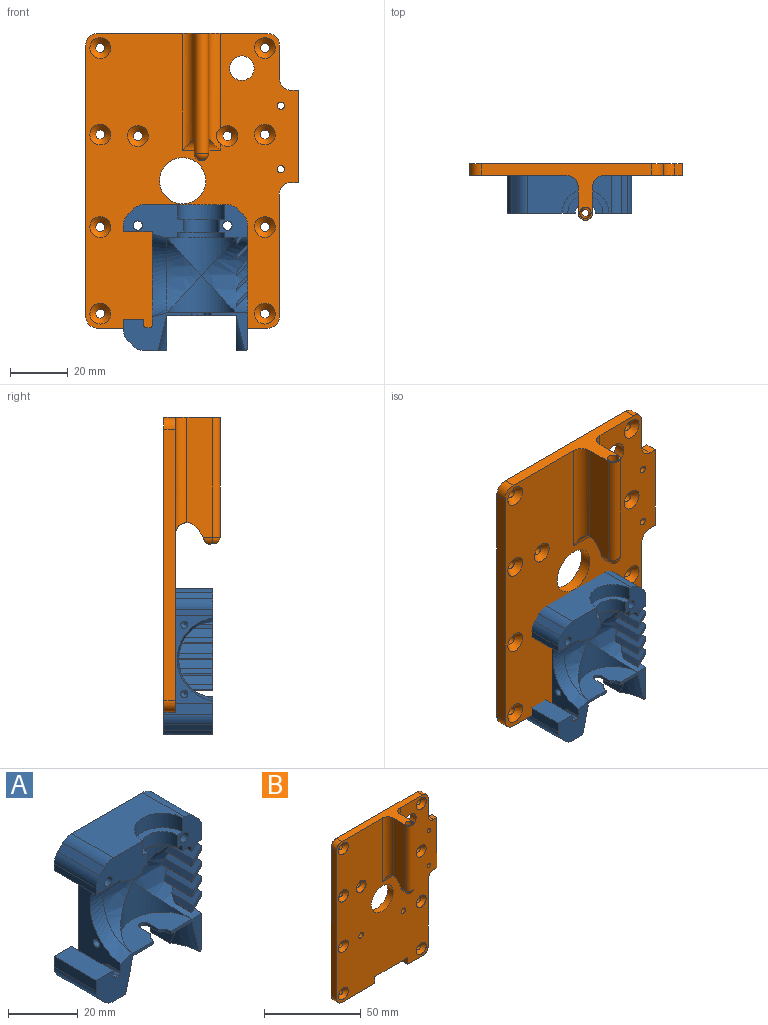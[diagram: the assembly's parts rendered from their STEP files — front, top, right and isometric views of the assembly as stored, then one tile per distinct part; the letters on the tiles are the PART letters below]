
ASSEMBLY  parts=2 mates=1
PART A: 86 faces, bbox 47x25.3x54.5 mm
  f0: cone r=0mm half-angle=59deg, axis (-1,0,0), area 5.7mm2, adj f9
  f1: cone r=0mm half-angle=59deg, axis (-1,0,0), area 5.7mm2, adj f10
  f2: plane 6.9x1mm, normal (0,1,0), area 6.9mm2, adj f8,f12,f15,f43
  f3: cylinder r=12mm len=24mm, axis (0,0,1), area 245mm2, adj f11,f20,f77
  f4: cylinder r=12mm len=24mm, axis (0,0,1), area 245mm2, adj f11,f65,f77
  f5: plane 4.29x1mm, normal (1,0,0), area 4.3mm2, adj f6,f17,f18,f20
  f6: cylinder r=1.6mm len=3.2mm, axis (0,0,1), area 5mm2, adj f5,f7,f17,f20
  f7: plane 4.29x1mm, normal (-1,0,0), area 4.3mm2, adj f6,f17,f19,f20
  f8: cylinder r=1mm len=6.9mm, axis (0,0,1), area 10.8mm2, adj f2,f27,f41,f43
  f9: cylinder r=1.25mm len=5mm, axis (-1,0,0), area 39.3mm2, adj f0,f41
  f10: cylinder r=1.25mm len=5mm, axis (-1,0,0), area 39.3mm2, adj f1,f41
  f11: extruded ~26x12mm, area 239.5mm2, adj f3,f4,f33
  f12: cylinder r=1mm len=1mm, axis (1,0,0), area 1.6mm2, adj f2,f26,f27,f40
  f13: plane 20.95x15.95mm, normal (1,0,0), area 133.6mm2, adj f17,f23,f31,f43
  f14: plane 20.95x15.95mm, normal (-1,0,0), area 133.6mm2, adj f17,f23,f24,f25
  f15: cylinder r=1mm len=6.9mm, axis (0,0,1), area 10.8mm2, adj f2,f26,f35,f38,f43
  f16: plane 10.9x7mm, normal (0,1,0), area 62.7mm2, adj f34,f35,f36,f38,f42,f76
  f17: plane 24x17mm, normal (0,0,-1), area 371.9mm2, adj f5,f6,f7,f13,f14,f18,f19,f23
  f18: cylinder r=3.5mm len=3.11mm, axis (0,0,1), area 3.8mm2, adj f5,f17,f20,f83
  f19: cylinder r=3.5mm len=3.11mm, axis (0,0,1), area 3.8mm2, adj f7,f17,f20,f84
  f20: plane 24x12mm, normal (0,0,1), area 190mm2, adj f3,f5,f6,f7,f18,f19,f83,f84
  f21: cylinder r=1.6mm len=17mm, axis (0,1,0), area 170.9mm2, adj f23,f85
  f22: cylinder r=1.6mm len=17mm, axis (0,1,0), area 170.9mm2, adj f23,f82
  f23: plane 50.5x43mm, normal (0,1,0), area 1429mm2, adj f13,f14,f17,f21,f22,f25,f32,f41
  f24: cone r=12mm half-angle=14deg, axis (0,0,-1), area 55.7mm2, adj f14,f25,f84
  f25: plane 17x3mm, normal (0,0,-1), area 32.6mm2, adj f14,f23,f24,f44
  f26: torus R=2mm, axis (1,0,0), area 3.4mm2, adj f12,f15,f37,f38
  f27: torus R=2mm, axis (-1,0,0), area 3.4mm2, adj f8,f12,f39,f41
  f28: plane 6.65x2.17mm, normal (0.71,0,-0.71), area 13.8mm2, adj f29,f77,f82
  f29: plane 6.64x1.41mm, normal (-1,0,0), area 7.7mm2, adj f28,f30,f77,f82
  f30: plane 4.41x1.13mm, normal (-0.71,0,0.71), area 2.9mm2, adj f29,f77,f82
  f31: cone r=12mm half-angle=14deg, axis (0,0,-1), area 55.7mm2, adj f13,f43,f83
  f32: plane 17x10mm, normal (0,0,-1), area 170mm2, adj f23,f41,f75,f85
  f33: bspline ~28.84x16.7mm, area 203.5mm2, adj f11,f41,f83,f85
  f34: cylinder r=5mm len=17mm, axis (0,-1,0), area 66.8mm2, adj f16,f36,f42,f83
  f35: cylinder r=5mm len=17mm, axis (0,1,0), area 66mm2, adj f15,f16,f36,f38,f43,f83
  f36: plane 17x2.07mm, normal (-0.71,0,-0.71), area 49.8mm2, adj f16,f34,f35,f83
  f37: cylinder r=1mm len=5mm, axis (0,1,0), area 7.9mm2, adj f26,f38,f40,f83
  f38: plane 17x10.9mm, normal (1,0,0), area 123.9mm2, adj f15,f16,f26,f35,f37,f76,f83
  f39: cylinder r=1mm len=5mm, axis (0,1,0), area 7.9mm2, adj f27,f40,f41,f83
  f40: plane 5x1mm, normal (0,0,1), area 5mm2, adj f12,f37,f39,f83
  f41: plane 41.1x17.03mm, normal (-1,0,0), area 357.9mm2, adj f8,f9,f10,f23,f27,f32,f33,f39
  f42: plane 17x3.83mm, normal (-1,0,0), area 65.1mm2, adj f16,f34,f76,f83
  f43: plane 17x7.93mm, normal (0,0,-1), area 84.6mm2, adj f2,f8,f13,f15,f23,f31,f35,f41
  f44: cylinder r=1mm len=17mm, axis (0,-1,0), area 26.7mm2, adj f23,f25,f64,f84
  f45: plane 10.55x4.34mm, normal (0.71,0,-0.71), area 49.1mm2, adj f48,f64,f77,f78
  f46: plane 8.95x1.74mm, normal (-0.92,0,0.38), area 15mm2, adj f47,f48,f77,f78
  f47: plane 11.04x3.42mm, normal (-0.71,0,0.71), area 46.7mm2, adj f46,f64,f77,f78
  f48: plane 7.18x0.41mm, normal (-1,0,0), area 2.9mm2, adj f45,f46,f77,f78
  f49: plane 11.62x1.72mm, normal (-0.92,0,0.38), area 21mm2, adj f50,f52,f77,f79
  f50: plane 12.02x3.31mm, normal (-0.71,0,0.71), area 55.3mm2, adj f49,f64,f77,f79
  f51: plane 11.99x4.07mm, normal (0.71,0,-0.71), area 65.2mm2, adj f52,f64,f77,f79
  f52: plane 11.08x0.41mm, normal (-1,0,0), area 4.6mm2, adj f49,f51,f77,f79
  f53: plane 12.04x4.04mm, normal (0.71,0,-0.71), area 66.8mm2, adj f55,f64,f77,f80
  f54: plane 12x1.71mm, normal (-0.92,0,0.38), area 22.1mm2, adj f55,f56,f77,f80
  f55: plane 12x0.41mm, normal (-1,0,0), area 5mm2, adj f53,f54,f77,f80
  f56: plane 11.89x3.34mm, normal (-0.71,0,0.71), area 53.3mm2, adj f54,f64,f77,f80
  f57: plane 11.12x4.21mm, normal (0.71,0,-0.71), area 55.3mm2, adj f59,f64,f77,f81
  f58: plane 10.74x1.72mm, normal (-0.92,0,0.38), area 19mm2, adj f59,f60,f77,f81
  f59: plane 10.91x0.41mm, normal (-1,0,0), area 4.5mm2, adj f57,f58,f77,f81
  f60: plane 10.03x3.55mm, normal (-0.71,0,0.71), area 39.1mm2, adj f58,f64,f77,f81
  f61: cylinder r=5mm len=17mm, axis (0,1,0), area 66.8mm2, adj f23,f63,f64,f82
  f62: cylinder r=5mm len=17mm, axis (0,-1,0), area 66.8mm2, adj f23,f63,f74,f82
  f63: plane 17x2.07mm, normal (0.71,0,0.71), area 49.8mm2, adj f23,f61,f62,f82
  f64: plane 42.43x17mm, normal (1,0,0), area 534.6mm2, adj f23,f44,f45,f47,f50,f51,f53,f56
  f65: plane 24x12mm, normal (0,0,-1), area 123.1mm2, adj f4,f67,f82,f85
  f66: plane 16.2x8.1mm, normal (0,0,-1), area 44.6mm2, adj f67,f68,f82,f85
  f67: cylinder r=8.1mm len=16.2mm, axis (0,0,1), area 50.9mm2, adj f65,f66,f82,f85
  f68: cylinder r=6.1mm len=12.2mm, axis (0,0,1), area 86.2mm2, adj f66,f69,f82,f85
  f69: plane 16.2x8.1mm, normal (0,0,1), area 44.6mm2, adj f68,f70,f82,f85
  f70: cylinder r=8.1mm len=16.2mm, axis (0,0,1), area 127.2mm2, adj f69,f74,f82,f85
  f71: cylinder r=5mm len=17mm, axis (0,-1,0), area 66.8mm2, adj f23,f73,f74,f85
  f72: cylinder r=5mm len=17mm, axis (0,-1,0), area 66.8mm2, adj f23,f73,f75,f85
  f73: plane 17x2.07mm, normal (-0.71,0,0.71), area 49.8mm2, adj f23,f71,f72,f85
  f74: plane 28.86x17mm, normal (0,0,1), area 387.5mm2, adj f23,f62,f70,f71,f82,f85
  f75: plane 17x2.33mm, normal (-1,0,0), area 39.6mm2, adj f23,f32,f72,f85
  f76: plane 17x7mm, normal (0,0,1), area 119mm2, adj f16,f38,f42,f83
  f77: extruded ~26x16mm, area 298.8mm2, adj f3,f4,f28,f29,f30,f45,f46,f47
  f78: plane 5.41x4mm, normal (0,-1,0), area 5.3mm2, adj f45,f46,f47,f48,f64
  f79: plane 5.41x4mm, normal (0,-1,0), area 5.3mm2, adj f49,f50,f51,f52,f64
  f80: plane 5.41x4mm, normal (0,-1,0), area 5.3mm2, adj f53,f54,f55,f56,f64
  f81: plane 5.41x4mm, normal (0,-1,0), area 5.3mm2, adj f57,f58,f59,f60,f64
  f82: plane 13.67x9.9mm, normal (0,-1,0), area 80.3mm2, adj f22,f28,f29,f30,f61,f62,f63,f64
  f83: plane 23.87x13.37mm, normal (0,-1,0), area 139mm2, adj f17,f18,f20,f31,f33,f34,f35,f36
  f84: plane 13x12.5mm, normal (0,-1,0), area 42.3mm2, adj f17,f19,f20,f24,f44,f64,f77
  f85: plane 20.91x11.51mm, normal (0,-1,0), area 180.4mm2, adj f21,f32,f33,f41,f65,f66,f67,f68
PART B: 59 faces, bbox 73.5x19.5x102 mm
  f0: cylinder r=2.5mm len=3.39mm, axis (0,-1,0), area 7.8mm2, adj f1,f49,f54,f56,f57
  f1: plane 41.5x9mm, normal (-1,0,0), area 354mm2, adj f0,f7,f49,f51,f52,f53
  f2: plane 41.5x9mm, normal (1,0,0), area 354mm2, adj f7,f49,f50,f52,f53,f55
  f3: plane 102x73.5mm, normal (0,-1,0), area 5720.8mm2, adj f4,f5,f6,f7,f8,f9,f10,f11
  f4: plane 42.41x4mm, normal (1,0,0), area 169.6mm2, adj f3,f29,f31,f48
  f5: plane 11.59x4mm, normal (1,0,0), area 46.4mm2, adj f3,f6,f31,f47
  f6: cylinder r=4mm len=4mm, axis (0,1,0), area 25.1mm2, adj f3,f5,f7,f31
  f7: plane 59x19.5mm, normal (0,0,1), area 305.8mm2, adj f1,f2,f3,f6,f8,f31,f50,f51
  f8: cylinder r=4mm len=4mm, axis (0,1,0), area 25.1mm2, adj f3,f7,f9,f31
  f9: plane 94x4mm, normal (-1,0,0), area 376mm2, adj f3,f8,f10,f31
  f10: cylinder r=4mm len=4mm, axis (0,1,0), area 25.1mm2, adj f3,f9,f11,f31
  f11: plane 24x4mm, normal (0,0,-1), area 96mm2, adj f3,f10,f12,f31
  f12: plane 4.25x4mm, normal (1,0,0), area 17mm2, adj f3,f11,f13,f31
  f13: plane 24x4mm, normal (0,0,-1), area 96mm2, adj f3,f12,f14,f31
  f14: plane 4.25x4mm, normal (-1,0,0), area 17mm2, adj f3,f13,f15,f31
  f15: plane 11x4mm, normal (0,0,-1), area 44mm2, adj f3,f14,f29,f31
  f16: cylinder r=1.6mm len=4mm, axis (0,1,0), area 40.2mm2, adj f3,f31
  f17: cylinder r=1.6mm len=4mm, axis (0,1,0), area 40.2mm2, adj f3,f31
  f18: cylinder r=1.6mm len=3.2mm, axis (0,1,0), area 20.1mm2, adj f31,f38
  f19: cylinder r=1.6mm len=3.2mm, axis (0,1,0), area 20.1mm2, adj f31,f37
  f20: cylinder r=1.6mm len=3.2mm, axis (0,1,0), area 20.1mm2, adj f31,f41
  f21: cylinder r=1.6mm len=3.2mm, axis (0,1,0), area 20.1mm2, adj f31,f36
  f22: cylinder r=1.6mm len=3.2mm, axis (0,1,0), area 20.1mm2, adj f31,f35
  f23: cylinder r=1.6mm len=3.2mm, axis (0,1,0), area 20.1mm2, adj f31,f34
  f24: cylinder r=1.6mm len=3.2mm, axis (0,1,0), area 20.1mm2, adj f31,f33
  f25: cylinder r=1.6mm len=3.2mm, axis (0,1,0), area 20.1mm2, adj f31,f32
  f26: cylinder r=1.6mm len=3.2mm, axis (0,1,0), area 20.1mm2, adj f31,f39
  f27: cylinder r=1.6mm len=3.2mm, axis (0,1,0), area 20.1mm2, adj f31,f40
  f28: cylinder r=8mm len=16mm, axis (0,1,0), area 201.1mm2, adj f3,f31
  f29: cylinder r=4mm len=4mm, axis (0,1,0), area 25.1mm2, adj f3,f4,f15,f31
  f30: cylinder r=4.25mm len=8.5mm, axis (0,1,0), area 106.8mm2, adj f3,f31
  f31: plane 102x73.5mm, normal (0,1,0), area 6569mm2, adj f4,f5,f6,f7,f8,f9,f10,f11
  f32: cone r=1.6mm half-angle=45deg, axis (0,-1,0), area 46.2mm2, adj f3,f25
  f33: cone r=1.6mm half-angle=45deg, axis (0,-1,0), area 46.2mm2, adj f3,f24
  f34: cone r=1.6mm half-angle=45deg, axis (0,-1,0), area 46.2mm2, adj f3,f23
  f35: cone r=1.6mm half-angle=45deg, axis (0,-1,0), area 46.2mm2, adj f3,f22
  f36: cone r=1.6mm half-angle=45deg, axis (0,-1,0), area 46.2mm2, adj f3,f21
  f37: cone r=1.6mm half-angle=45deg, axis (0,-1,0), area 46.2mm2, adj f3,f19
  f38: cone r=1.6mm half-angle=45deg, axis (0,-1,0), area 47.1mm2, adj f3,f18,f50
  f39: cone r=1.6mm half-angle=45deg, axis (0,-1,0), area 46.2mm2, adj f3,f26
  f40: cone r=1.6mm half-angle=45deg, axis (0,-1,0), area 46.2mm2, adj f3,f27
  f41: cone r=1.6mm half-angle=45deg, axis (0,-1,0), area 46.2mm2, adj f3,f20
  f42: plane 4x2.5mm, normal (0,0,1), area 10mm2, adj f3,f31,f43,f47
  f43: plane 32x4mm, normal (1,0,0), area 128mm2, adj f3,f31,f42,f44
  f44: plane 4x2.5mm, normal (0,0,-1), area 10mm2, adj f3,f31,f43,f48
  f45: cylinder r=1.25mm len=4mm, axis (0,-1,0), area 31.4mm2, adj f3,f31
  f46: cylinder r=1.25mm len=4mm, axis (0,-1,0), area 31.4mm2, adj f3,f31
  f47: cylinder r=4mm len=4mm, axis (0,1,0), area 25.1mm2, adj f3,f5,f31,f42
  f48: cylinder r=4mm len=4mm, axis (0,-1,0), area 25.1mm2, adj f3,f4,f31,f44
  f49: cylinder r=13.51mm len=5mm, axis (-1,0,0), area 29.2mm2, adj f0,f1,f2,f52,f55,f56
  f50: cylinder r=4mm len=40.42mm, axis (0,0,1), area 233.3mm2, adj f2,f3,f7,f38,f52
  f51: cylinder r=4mm len=40.42mm, axis (0,0,-1), area 238mm2, adj f1,f3,f7,f52
  f52: cylinder r=4mm len=13mm, axis (-1,0,0), area 65.1mm2, adj f1,f2,f3,f49,f50,f51
  f53: cylinder r=2.5mm len=41.5mm, axis (0,0,-1), area 325.9mm2, adj f1,f2,f7,f54
  f54: sphere r=2.5mm, area 17mm2, adj f0,f53,f55,f57
  f55: cylinder r=2.5mm len=3.39mm, axis (0,-1,0), area 7.8mm2, adj f2,f49,f54,f56,f57
  f56: cylinder r=2.5mm len=4.67mm, axis (-1,0,0), area 7.7mm2, adj f0,f49,f55,f57
  f57: cylinder r=1.25mm len=23.95mm, axis (0,0,1), area 186.6mm2, adj f0,f54,f55,f56,f58
  f58: cone r=1.25mm half-angle=2deg, axis (0,0,1), area 201.1mm2, adj f7,f57
PLACE A t=(-138.01,-286.8,-86.11)mm
PLACE B t=(-144.51,-282.8,-70.61)mm
MATE cylindrical B.f17 <-> A.f22  axis (0,1,0) through (-129.01,-282.8,-86.11)mm
